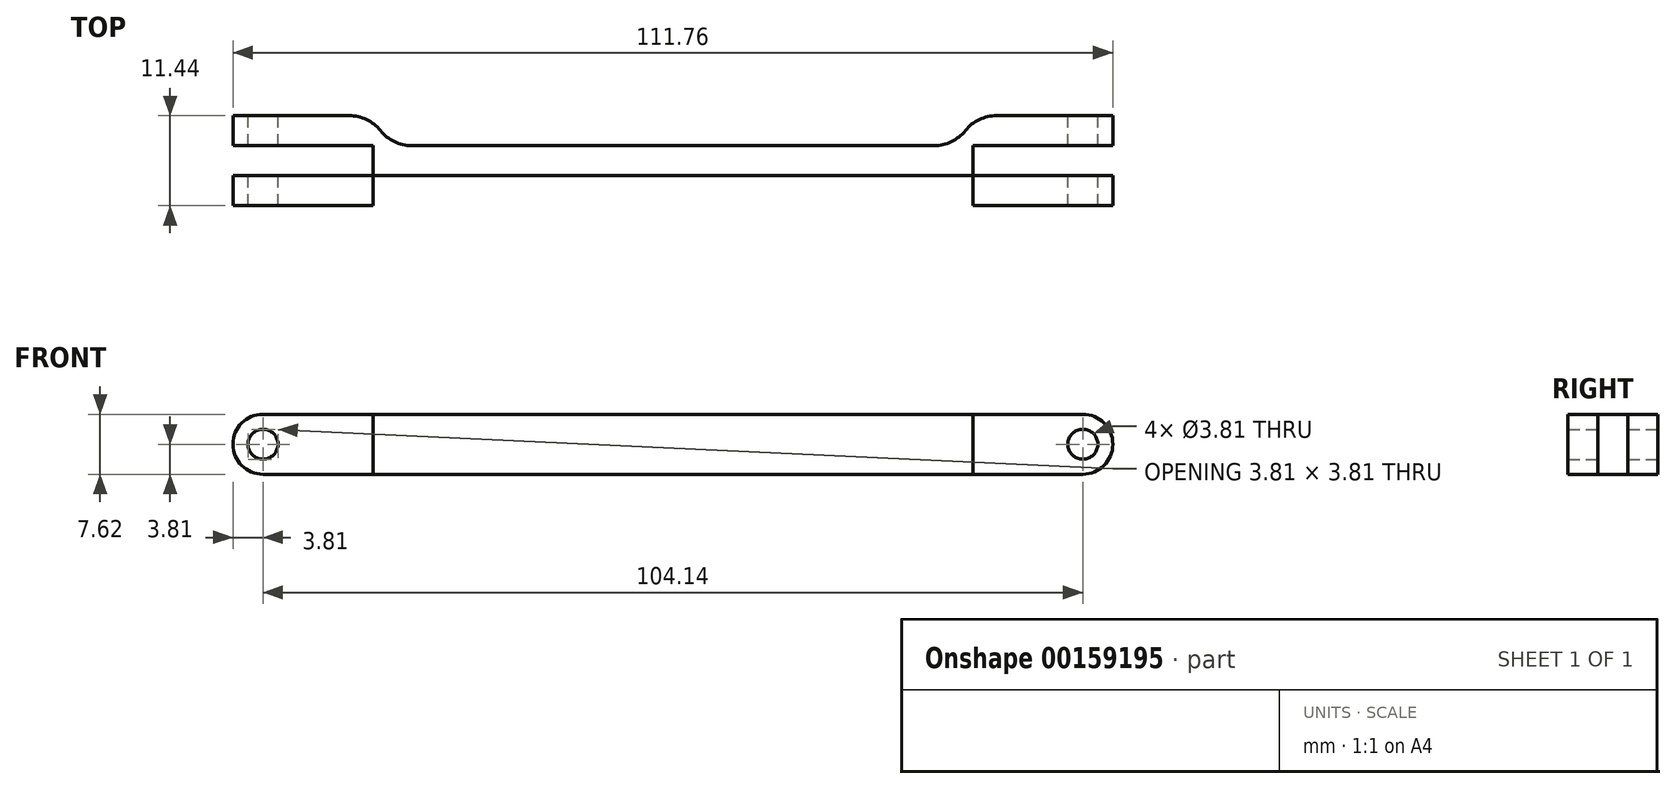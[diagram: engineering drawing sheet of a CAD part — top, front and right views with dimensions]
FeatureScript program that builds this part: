
annotation { "Feature Type Name" : "Feature", "Feature Type Description" : "" }
export const myFeature = defineFeature(function(context is Context, id is Id, definition is map)
    precondition{}
    {
        {
            var Q0;
            Q0=qCreatedBy(makeId("Front.planeOp"),FACE);
            var sketch = newSketch(context, id + "F0", { "sketchPlane" : qUnion([Q0])});
            skLineSegment(sketch, "E0.bottom", {"start": v(-38.1, 3.81) * mm, "end": v(38.1, 3.81) * mm});
            skLineSegment(sketch, "E0.top", {"start": v(-38.1, -3.8) * mm, "end": v(38.1, -3.8) * mm});
            skLineSegment(sketch, "E0.left", {"start": v(-38.1, 3.81) * mm, "end": v(-38.1, -3.8) * mm});
            skLineSegment(sketch, "E0.right", {"start": v(38.1, 3.81) * mm, "end": v(38.1, -3.8) * mm});
            skPoint(sketch, "E0.middle", {"position": v(0, 0) * mm});
            skSolve(sketch);
        }
        {
            var Q0;
            Q0=makeQuery(id+"F0.imprint","IMPRINT",FACE,{"disambiguationData":[TD([[makeQuery(id+"F0.imprint","IMPRINT",EDGE,{"derivedFrom":sQuery(id+"F0.wireOp",EDGE,"E0.bottom")}),-1.0]])]});
            extrude(context, id + "F1", {"entities" : qUnion([Q0]), "endBound" : BoundingType.SYMMETRIC, "depth" : 3.8 * mm});
        }
        {
            var Q0;
            Q0=qCreatedBy(makeId("Front.planeOp"),FACE);
            var sketch = newSketch(context, id + "F2", { "sketchPlane" : qUnion([Q0])});
            skLineSegment(sketch, "E1", {"start": v(0, 0) * mm, "end": v(0, 3.22) * mm, "construction": true});
            skLineSegment(sketch, "E2.bottom", {"start": v(38.1, -3.8) * mm, "end": v(52.07, -3.8) * mm});
            skLineSegment(sketch, "E2.top", {"start": v(38.1, 3.8) * mm, "end": v(52.07, 3.8) * mm});
            skLineSegment(sketch, "E2.left", {"start": v(38.1, -3.8) * mm, "end": v(38.1, 3.81) * mm});
            skLineSegment(sketch, "E2.right", {"start": v(55.88, 0) * mm, "end": v(55.88, 0) * mm});
            skPoint(sketch, "E3.visualSharp", {"position": v(55.88, 3.81) * mm});
            skArc(sketch, "E3.filletArc", {"start": v(55.88, 0) * mm, "mid": v(54.76, 2.7) * mm, "end": v(52.07, 3.8) * mm});
            skPoint(sketch, "E4.visualSharp", {"position": v(55.88, -3.8) * mm});
            skArc(sketch, "E4.filletArc", {"start": v(52.07, -3.8) * mm, "mid": v(54.76, -2.7) * mm, "end": v(55.88, 0) * mm});
            skCircle(sketch, "E5", {"center": v(52.07, 0) * mm, "radius": 1.9 * mm});
            skLineSegment(sketch, "E6.MirrorCS", {"start": v(-38.1, 3.8) * mm, "end": v(-52.07, 3.8) * mm});
            skLineSegment(sketch, "E7.MirrorCS", {"start": v(-38.1, -3.8) * mm, "end": v(-38.1, 3.81) * mm});
            skLineSegment(sketch, "E8.MirrorCS", {"start": v(-38.1, -3.8) * mm, "end": v(-52.07, -3.8) * mm});
            skCircle(sketch, "E9.MirrorC", {"center": v(-52.07, 0) * mm, "radius": 1.9 * mm});
            skArc(sketch, "E10.MirrorCS", {"start": v(-52.07, -3.8) * mm, "mid": v(-54.76, -2.7) * mm, "end": v(-55.88, 0) * mm});
            skArc(sketch, "E11.MirrorCS", {"start": v(-55.88, 0) * mm, "mid": v(-54.76, 2.7) * mm, "end": v(-52.07, 3.8) * mm});
            skSolve(sketch);
        }
        {
            var Q0;
            Q0=makeQuery(id+"F2.imprint","IMPRINT",FACE,{"disambiguationData":[TD([[makeQuery(id+"F2.imprint","IMPRINT",EDGE,{"derivedFrom":sQuery(id+"F2.wireOp",EDGE,"E6.MirrorCS")}),1.0]])]});
            var Q1;
            Q1=makeQuery(id+"F2.imprint","IMPRINT",FACE,{"disambiguationData":[TD([[makeQuery(id+"F2.imprint","IMPRINT",EDGE,{"derivedFrom":sQuery(id+"F2.wireOp",EDGE,"E2.bottom")}),1.0]])]});
            extrude(context, id + "F3", {"entities" : qUnion([Q0, Q1]), "operationType" : NewBodyOperationType.ADD, "endBound" : BoundingType.SYMMETRIC, "depth" : 11.43 * mm});
        }
        {
            var Q0;
            Q0=makeQuery(id+"F1.opExtrude","CAP_EDGE",EDGE,{"disambiguationData":[OSD([sQuery(id+"F0.wireOp",EDGE,"E0.left")])],"isStart":false});
            var Q1;
            Q1=makeQuery(id+"F1.opExtrude","CAP_EDGE",EDGE,{"disambiguationData":[OSD([sQuery(id+"F0.wireOp",EDGE,"E0.right")])],"isStart":false});
            var Q2;
            Q2=makeQuery(id+"F1.opExtrude","CAP_EDGE",EDGE,{"disambiguationData":[OSD([sQuery(id+"F0.wireOp",EDGE,"E0.right")])],"isStart":true});
            var Q3;
            Q3=makeQuery(id+"F1.opExtrude","CAP_EDGE",EDGE,{"disambiguationData":[OSD([sQuery(id+"F0.wireOp",EDGE,"E0.left")])],"isStart":true});
            fillet(context, id + "F4", {"entities" : qUnion([Q0, Q1, Q2, Q3]), "radius" : 5.08 * mm, "tangentPropagation" : true, "allowEdgeOverflow" : false});
        }
        {
            var Q0;
            Q0=makeQuery(id+"F3.boolean.opBoolean","MERGE",FACE,{"derivedFrom":[makeQuery(id+"F1.opExtrude","SWEPT_FACE",FACE,{"disambiguationData":[OSD([sQuery(id+"F0.wireOp",EDGE,"E0.bottom")])]}),makeQuery(id+"F3.opExtrude","SWEPT_FACE",FACE,{"disambiguationData":[OSD([sQuery(id+"F2.wireOp",EDGE,"E2.top")])]}),makeQuery(id+"F3.opExtrude","SWEPT_FACE",FACE,{"disambiguationData":[OSD([sQuery(id+"F2.wireOp",EDGE,"E6.MirrorCS")])]})]});
            var sketch = newSketch(context, id + "F5", { "sketchPlane" : qUnion([Q0])});
            skLineSegment(sketch, "E12.bottom", {"start": v(-38.1, 1.9) * mm, "end": v(-70.67, 1.9) * mm});
            skLineSegment(sketch, "E12.top", {"start": v(-38.1, -1.9) * mm, "end": v(-70.67, -1.9) * mm});
            skLineSegment(sketch, "E12.left", {"start": v(-38.1, 1.9) * mm, "end": v(-38.1, -1.9) * mm});
            skLineSegment(sketch, "E12.right", {"start": v(-70.67, 1.9) * mm, "end": v(-70.67, -1.9) * mm});
            skLineSegment(sketch, "E13", {"start": v(0, 0) * mm, "end": v(0, 4.63) * mm, "construction": true});
            skPoint(sketch, "E13.endSnap0", {"position": v(0, 1.9) * mm});
            skLineSegment(sketch, "E14.MirrorCS", {"start": v(70.67, 1.9) * mm, "end": v(70.67, -1.9) * mm});
            skLineSegment(sketch, "E15.MirrorCS", {"start": v(38.1, 1.9) * mm, "end": v(70.67, 1.9) * mm});
            skLineSegment(sketch, "E16.MirrorCS", {"start": v(38.1, -1.9) * mm, "end": v(70.67, -1.9) * mm});
            skLineSegment(sketch, "E17.MirrorCS", {"start": v(38.1, 1.9) * mm, "end": v(38.1, -1.9) * mm});
            skSolve(sketch);
        }
        {
            var Q0;
            Q0 = qSketchRegion(id + "F5", true);
            extrude(context, id + "F6", {"entities" : qUnion([Q0]), "operationType" : NewBodyOperationType.REMOVE, "endBound" : BoundingType.THROUGH_ALL, "oppositeDirection" : true, "depth" : 25.4 * mm});
        }
        {
            var Q0;
            Q0=makeQuery(id+"F4.opFillet","BLEND_EDGE",EDGE,{"blendedFrom":[makeQuery(id+"F1.opExtrude","CAP_EDGE",EDGE,{"disambiguationData":[OSD([sQuery(id+"F0.wireOp",EDGE,"E0.left")])],"isStart":false}),makeQuery(id+"F3.opExtrude","CAP_FACE",FACE,{"disambiguationData":[OSD([sQuery(id+"F2.wireOp",EDGE,"E6.MirrorCS"),sQuery(id+"F2.wireOp",EDGE,"E7.MirrorCS"),sQuery(id+"F2.wireOp",EDGE,"E8.MirrorCS"),sQuery(id+"F2.wireOp",EDGE,"E9.MirrorC"),sQuery(id+"F2.wireOp",EDGE,"E10.MirrorCS"),sQuery(id+"F2.wireOp",EDGE,"E11.MirrorCS")])],"isStart":false})],"blendedInto":[makeQuery(id+"F3.opExtrude","CAP_FACE",FACE,{"disambiguationData":[OSD([sQuery(id+"F2.wireOp",EDGE,"E6.MirrorCS"),sQuery(id+"F2.wireOp",EDGE,"E7.MirrorCS"),sQuery(id+"F2.wireOp",EDGE,"E8.MirrorCS"),sQuery(id+"F2.wireOp",EDGE,"E9.MirrorC"),sQuery(id+"F2.wireOp",EDGE,"E10.MirrorCS"),sQuery(id+"F2.wireOp",EDGE,"E11.MirrorCS")])],"isStart":false})]});
            var Q1;
            Q1=makeQuery(id+"F4.opFillet","BLEND_EDGE",EDGE,{"blendedFrom":[makeQuery(id+"F1.opExtrude","CAP_EDGE",EDGE,{"disambiguationData":[OSD([sQuery(id+"F0.wireOp",EDGE,"E0.left")])],"isStart":true}),makeQuery(id+"F3.opExtrude","CAP_FACE",FACE,{"disambiguationData":[OSD([sQuery(id+"F2.wireOp",EDGE,"E6.MirrorCS"),sQuery(id+"F2.wireOp",EDGE,"E7.MirrorCS"),sQuery(id+"F2.wireOp",EDGE,"E8.MirrorCS"),sQuery(id+"F2.wireOp",EDGE,"E9.MirrorC"),sQuery(id+"F2.wireOp",EDGE,"E10.MirrorCS"),sQuery(id+"F2.wireOp",EDGE,"E11.MirrorCS")])],"isStart":true})],"blendedInto":[makeQuery(id+"F3.opExtrude","CAP_FACE",FACE,{"disambiguationData":[OSD([sQuery(id+"F2.wireOp",EDGE,"E6.MirrorCS"),sQuery(id+"F2.wireOp",EDGE,"E7.MirrorCS"),sQuery(id+"F2.wireOp",EDGE,"E8.MirrorCS"),sQuery(id+"F2.wireOp",EDGE,"E9.MirrorC"),sQuery(id+"F2.wireOp",EDGE,"E10.MirrorCS"),sQuery(id+"F2.wireOp",EDGE,"E11.MirrorCS")])],"isStart":true})]});
            var Q2;
            Q2=makeQuery(id+"F4.opFillet","BLEND_EDGE",EDGE,{"blendedFrom":[makeQuery(id+"F1.opExtrude","CAP_EDGE",EDGE,{"disambiguationData":[OSD([sQuery(id+"F0.wireOp",EDGE,"E0.right")])],"isStart":false}),makeQuery(id+"F3.opExtrude","CAP_FACE",FACE,{"disambiguationData":[OSD([sQuery(id+"F2.wireOp",EDGE,"E2.bottom"),sQuery(id+"F2.wireOp",EDGE,"E2.top"),sQuery(id+"F2.wireOp",EDGE,"E2.left"),sQuery(id+"F2.wireOp",EDGE,"E3.filletArc"),sQuery(id+"F2.wireOp",EDGE,"E4.filletArc"),sQuery(id+"F2.wireOp",EDGE,"E5")])],"isStart":false})],"blendedInto":[makeQuery(id+"F3.opExtrude","CAP_FACE",FACE,{"disambiguationData":[OSD([sQuery(id+"F2.wireOp",EDGE,"E2.bottom"),sQuery(id+"F2.wireOp",EDGE,"E2.top"),sQuery(id+"F2.wireOp",EDGE,"E2.left"),sQuery(id+"F2.wireOp",EDGE,"E3.filletArc"),sQuery(id+"F2.wireOp",EDGE,"E4.filletArc"),sQuery(id+"F2.wireOp",EDGE,"E5")])],"isStart":false})]});
            var Q3;
            Q3=makeQuery(id+"F4.opFillet","BLEND_EDGE",EDGE,{"blendedFrom":[makeQuery(id+"F1.opExtrude","CAP_EDGE",EDGE,{"disambiguationData":[OSD([sQuery(id+"F0.wireOp",EDGE,"E0.right")])],"isStart":true}),makeQuery(id+"F3.opExtrude","CAP_FACE",FACE,{"disambiguationData":[OSD([sQuery(id+"F2.wireOp",EDGE,"E2.bottom"),sQuery(id+"F2.wireOp",EDGE,"E2.top"),sQuery(id+"F2.wireOp",EDGE,"E2.left"),sQuery(id+"F2.wireOp",EDGE,"E3.filletArc"),sQuery(id+"F2.wireOp",EDGE,"E4.filletArc"),sQuery(id+"F2.wireOp",EDGE,"E5")])],"isStart":true})],"blendedInto":[makeQuery(id+"F3.opExtrude","CAP_FACE",FACE,{"disambiguationData":[OSD([sQuery(id+"F2.wireOp",EDGE,"E2.bottom"),sQuery(id+"F2.wireOp",EDGE,"E2.top"),sQuery(id+"F2.wireOp",EDGE,"E2.left"),sQuery(id+"F2.wireOp",EDGE,"E3.filletArc"),sQuery(id+"F2.wireOp",EDGE,"E4.filletArc"),sQuery(id+"F2.wireOp",EDGE,"E5")])],"isStart":true})]});
            fillet(context, id + "F7", {"entities" : qUnion([Q0, Q1, Q2, Q3]), "radius" : 5.08 * mm, "tangentPropagation" : true, "allowEdgeOverflow" : false});
        }
    });
